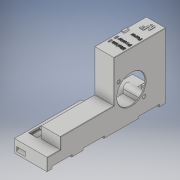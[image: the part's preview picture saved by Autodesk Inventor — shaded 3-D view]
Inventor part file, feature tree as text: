
AUTODESK INVENTOR PART (.ipt)
format: ipt  version: 2019 (Build 230136000, 136)  size: 2,290,176 bytes
history: native  units: mm
features: projected_geometry x47, extrude x32, sketch x32, chamfer x9, other x2, fillet x2, plane x1
ambient origin geometry x8: Origin, YZ Plane, XZ Plane, XY Plane, X Axis, Y Axis, Z Axis, Center Point
bodies: Volumenkörper1 (feature_tree)
feature tree (125):
  extrude  "Extrusion1"  Depth=32.0mm
  plane  "Arbeitsebene1"
  extrude  "Extrusion2"  [1 undecoded]
  extrude  "Extrusion3"  Depth=1.4mm
  extrude  "Extrusion4"  Depth=8.35mm TaperAngle=0.0deg
  extrude  "Extrusion5"  TaperAngle=0.0deg  [1 undecoded]
  extrude  "Extrusion6"  TaperAngle=45.0deg  [1 undecoded]
  extrude  "Extrusion7"  Depth=43.0mm
  extrude  "Extrusion9"  Depth=50.0mm
  extrude  "Extrusion10"  Depth=5.2mm
  extrude  "Extrusion11"  Depth=10.0mm TaperAngle=0.0deg
  sketch  "Skizze14"  dims[d30=4.5mm d33=10.0mm d34=0.0mm]
  other  "Prägen1"
  extrude  "Extrusion13"  Depth=2.4mm
  extrude  "Extrusion14"  Depth=1.5mm
  fillet  "Rundung2"  Radius=8.2mm
  chamfer  "Fase1"  Distance=10.0mm
  sketch  "Skizze17"  dims[d48=1.0mm d50=50.5mm]
  extrude  "Extrusion15"  Depth=1.0mm
  extrude  "Extrusion16"  Depth=1.0mm
  extrude  "Extrusion22"  Depth=10.0mm
  extrude  "Extrusion23"  Depth=1.0mm TaperAngle=0.0deg
  extrude  "Extrusion24"  Depth=2.7mm
  extrude  "Extrusion25"  Depth=1.0mm
  extrude  "Extrusion26"  Depth=5.0mm
  other  "Prägen2"
  chamfer  "Fase3"  Distance=10.0mm
  chamfer  "Fase5"  Distance=5.0mm
  extrude  "Extrusion27"  Depth=1.1mm
  extrude  "Extrusion28"  Depth=2.5mm
  extrude  "Extrusion29"  TaperAngle=0.0deg  [1 undecoded]
  chamfer  "Fase7"  Distance=1.5mm
  extrude  "Extrusion30"  Depth=2.5mm
  chamfer  "Fase8"  Distance=20.6mm
  extrude  "Extrusion31"  Depth=0.5mm TaperAngle=0.0deg
  extrude  "Extrusion32"  Depth=1.5mm
  extrude  "Extrusion33"  Depth=10.0mm
  extrude  "Extrusion34"  Depth=6.0mm
  fillet  "Rundung3"  Radius=10.0mm
  extrude  "Extrusion35"  Depth=10.0mm TaperAngle=0.0deg
  chamfer  "Fase11"  Distance=2.0mm
  extrude  "Extrusion36"  Depth=1.5mm TaperAngle=45.0deg
  chamfer  "Fase12"  Distance=0.4mm
  extrude  "Extrusion38"  Depth=10.0mm TaperAngle=0.0deg
  chamfer  "Fase13"  Distance=20.5mm
  extrude  "Extrusion37"  Depth=10.0mm
  chamfer  "Fase14"  Distance=45.0mm
  extrude  "Extrusion39"  Depth=10.0mm TaperAngle=0.0deg
  sketch  "Skizze2"  dims[d3=32.0mm d4=114.809mm]
  sketch  "Skizze3"  dims[d5=10.0mm d6=0.0mm d7=-21.5mm]
  projected_geometry  "Projizierte Kontur1"
  sketch  "Skizze4"  dims[d8=1.4mm d12=2.0mm]
  projected_geometry  "Projizierte Kontur2"
  sketch  "Skizze5"  dims[d13=15.0mm d14=8.35mm d15=0.0mm]
  projected_geometry  "Projizierte Kontur3"
  projected_geometry  "Projizierte Kontur4"
  sketch  "Skizze6"  dims[d16=7.0mm d17=0.0mm]
  projected_geometry  "Projizierte Kontur5"
  projected_geometry  "Projizierte Kontur6"
  projected_geometry  "Projizierte Kontur7"
  sketch  "Skizze8"  dims[d18=8.5mm d19=0.0mm d21=45.0deg]
  projected_geometry  "Projizierte Kontur8"
  sketch  "Skizze11"  dims[d22=30.0mm d23=43.0mm]
  projected_geometry  "Projizierte Kontur12"
  projected_geometry  "Projizierte Kontur13"
  projected_geometry  "Projizierte Kontur14"
  sketch  "Skizze12"  dims[d24=17.0mm d25=0.0mm d26=50.0mm]
  projected_geometry  "Projizierte Kontur15"
  sketch  "Skizze13"  dims[d27=16.0mm d28=0.0mm d29=5.2mm]
  projected_geometry  "Projizierte Kontur16"
  projected_geometry  "Projizierte Kontur17"
  projected_geometry  "Projizierte Kontur18"
  projected_geometry  "Projizierte Kontur19"
  sketch  "Skizze15"  dims[d35=2.1mm d36=2.4mm]
  projected_geometry  "Projizierte Kontur20"
  projected_geometry  "Projizierte Kontur21"
  sketch  "Skizze16"  dims[d37=1.5mm d38=1.5mm d39=8.2mm d40=10.0mm d41=0.0mm]
  projected_geometry  "Projizierte Kontur22"
  projected_geometry  "Projizierte Kontur23"
  sketch  "Skizze18"  dims[d51=1.0mm d52=1.0mm]
  projected_geometry  "Projizierte Kontur24"
  projected_geometry  "Projizierte Kontur25"
  projected_geometry  "Projizierte Kontur26"
  projected_geometry  "Projizierte Kontur27"
  projected_geometry  "Projizierte Kontur28"
  sketch  "Skizze19"  dims[d53=52.0mm d54=10.0mm]
  projected_geometry  "Projizierte Kontur29"
  sketch  "Skizze25"  dims[d55=18.6mm d56=0.0mm d58=1.0mm d59=0.0mm]
  projected_geometry  "Projizierte Kontur35"
  sketch  "Skizze26"  dims[d60=2.7mm d61=2.7mm]
  projected_geometry  "Projizierte Kontur36"
  sketch  "Skizze27"  dims[d62=100.0mm d63=1.0mm]
  projected_geometry  "Projizierte Kontur37"
  sketch  "Skizze28"  dims[d64=51.5mm d72=5.0mm]
  projected_geometry  "Projizierte Kontur38"
  projected_geometry  "Projizierte Kontur39"
  sketch  "Skizze29"  dims[d73=8.0mm]
  projected_geometry  "Projizierte Kontur40"
  sketch  "Skizze30"  dims[d74=5.2mm d76=10.0mm d77=0.0mm]
  projected_geometry  "Projizierte Kontur41"
  sketch  "Skizze31"  dims[d78=1.5mm]
  projected_geometry  "Projizierte Kontur42"
  sketch  "Skizze33"  dims[d79=1.5mm]
  projected_geometry  "Projizierte Kontur43"
  projected_geometry  "Projizierte Kontur44"
  sketch  "Skizze34"  dims[d80=1.0mm]
  projected_geometry  "Projizierte Kontur45"
  sketch  "Skizze35"  dims[d81=1.0mm]
  sketch  "Skizze36"  dims[d82=0.4mm]
  sketch  "Skizze37"  dims[d83=30.0mm]
  projected_geometry  "Projizierte Kontur46"
  projected_geometry  "Projizierte Kontur47"
  sketch  "Skizze38"  dims[d84=35.0mm]
  projected_geometry  "Projizierte Kontur48"
  sketch  "Skizze39"  dims[d85=3.0mm]
  projected_geometry  "Projizierte Kontur49"
  sketch  "Skizze41"  dims[d86=2.0mm]
  projected_geometry  "Projizierte Kontur51"
  sketch  "Skizze42"  dims[d88=10.0mm]
  projected_geometry  "Projizierte Kontur52"
  projected_geometry  "Projizierte Kontur53"
  projected_geometry  "Projizierte Kontur54"
  projected_geometry  "Projizierte Kontur55"
  sketch  "Skizze43"  dims[d89=3.0mm d90=5.0mm d95=1.1mm d96=2.5mm d97=0.0mm d98=1.5mm d99=2.5mm d100=20.6mm d103=0.5mm d104=0.0mm d105=1.5mm d106=11.0mm d107=6.0mm d108=10.0mm d109=0.0mm d110=10.0mm d111=0.0mm d112=2.0mm d113=1.5mm d114=2.0mm d115=45.0deg d116=0.4mm d119=10.0mm d120=0.0mm d122=20.5mm d123=14.0mm d126=45.0mm d127=4.3mm d128=0.0mm d151=2.2mm d152=0.0mm d164=10.0mm d165=4.5mm d167=3.335mm d168=7.0mm d169=0.0mm d171=8.0mm d173=20.0mm d174=10.0mm d175=10.0mm d176=10.0mm d177=0.0mm d178=1.0mm d179=0.3mm d180=10.0mm d181=0.0mm d182=0.4mm d183=0.0mm d184=0.4mm d185=0.0mm d189=0.4mm d190=2.0mm d191=45.0deg d195=0.4mm d196=2.0mm d197=45.0deg d198=10.0mm d199=25.0mm d200=3.0mm d201=3.0mm d202=5.0mm d203=5.0mm d204=5.0mm d205=5.0mm d206=10.0mm d207=0.0mm d211=0.8mm d212=1.0mm d213=0.0mm d214=0.0mm d215=10.0mm d216=10.0mm d217=0.5mm d218=0.5mm d219=5.0mm d220=0.0mm d221=0.4mm d222=2.0mm d223=45.0deg d224=4.0mm d225=10.0mm d226=0.0mm d227=0.8mm d228=2.0mm d229=45.0deg d230=1.8mm d231=2.5mm d233=3.0mm d234=0.0mm d238=3.0mm d239=0.0mm d240=1.5mm d241=7.0mm d242=7.0mm d243=10.0mm d244=0.0mm d245=2.6mm d246=2.6mm d247=2.6mm d248=4.0mm d249=4.0mm d250=5.0mm d251=3.0mm d252=5.0mm d253=30.0mm d254=10.0mm d255=0.0mm d256=7.0mm d257=2.6mm d258=4.0mm d259=4.0mm d260=6.0mm d264=5.0mm d265=1.6mm d266=0.0mm d267=0.4mm d268=2.0mm d269=45.0deg d270=0.2mm d271=0.0mm d272=1.5mm d273=2.0mm d274=45.0deg d275=0.4mm d276=0.3mm d277=0.4mm d278=0.3mm d279=12.0mm d280=0.0mm d281=3.5mm d282=10.0mm d283=0.0mm d284=1.0mm d285=2.0mm d286=45.0deg d287=0.35mm d288=2.0mm d289=45.0deg d290=1.8mm d291=1.5mm d292=3.5mm d293=3.5mm d294=10.0mm d295=0.0mm]
  projected_geometry  "Projizierte Kontur56"
note: 4 required parameter values undecoded (feature->parameter linkage not recoverable at this tier; creation-order binding heuristic only, values carry confidence <= 0.55)
